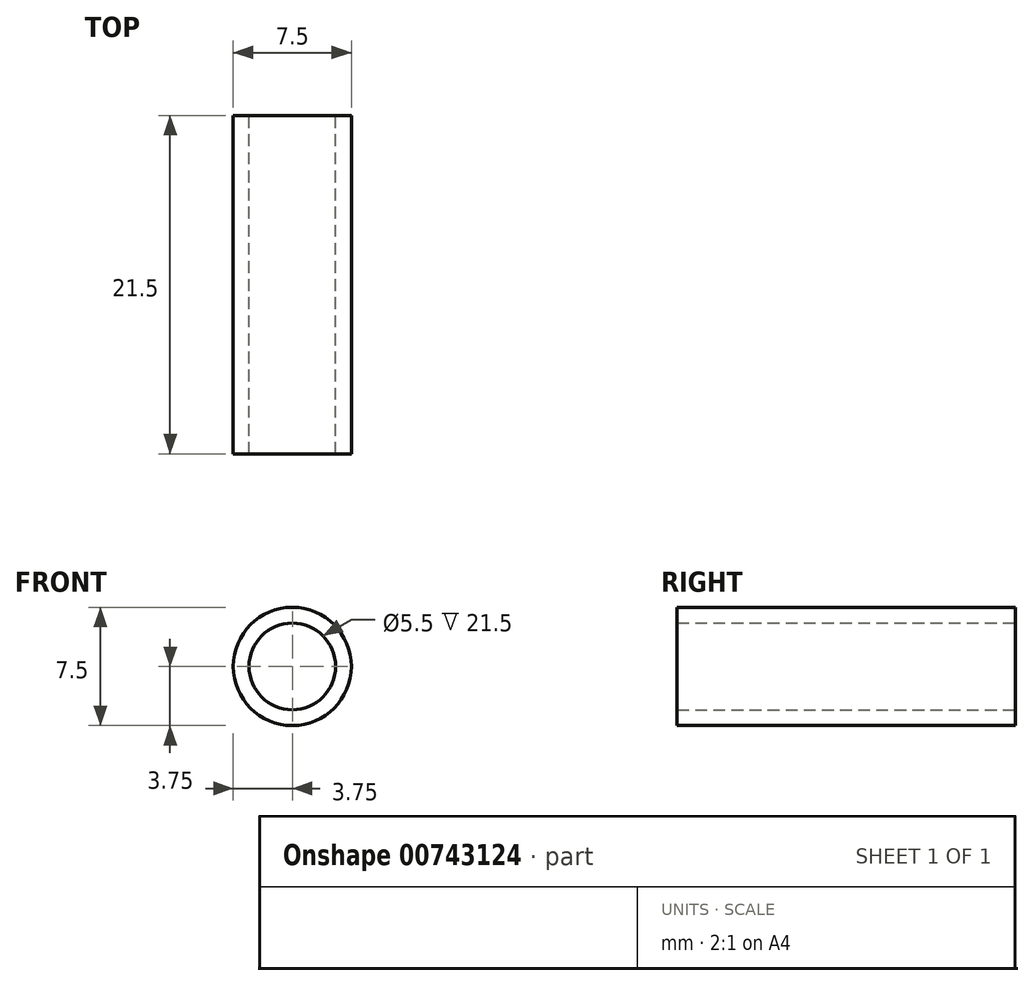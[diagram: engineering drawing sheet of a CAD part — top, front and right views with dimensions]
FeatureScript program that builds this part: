
annotation { "Feature Type Name" : "Feature", "Feature Type Description" : "" }
export const myFeature = defineFeature(function(context is Context, id is Id, definition is map)
    precondition{}
    {
        {
            var Q0;
            Q0=qCreatedBy(makeId("Front.planeOp"),FACE);
            var sketch = newSketch(context, id + "F0", { "sketchPlane" : qUnion([Q0])});
            skCircle(sketch, "E0", {"center": v(0, 0) * mm, "radius": 3.75 * mm});
            skCircle(sketch, "E1", {"center": v(0, 0) * mm, "radius": 2.75 * mm});
            skSolve(sketch);
        }
        {
            var Q0;
            Q0=makeQuery(id+"F0.imprint","IMPRINT",FACE,{"disambiguationData":[TD([[makeQuery(id+"F0.imprint","IMPRINT",EDGE,{"derivedFrom":sQuery(id+"F0.wireOp",EDGE,"E0")}),1.0]])]});
            extrude(context, id + "F1", {"entities" : qUnion([Q0]), "depth" : 21.5 * mm, "offsetDistance" : 25 * mm});
        }
    });
